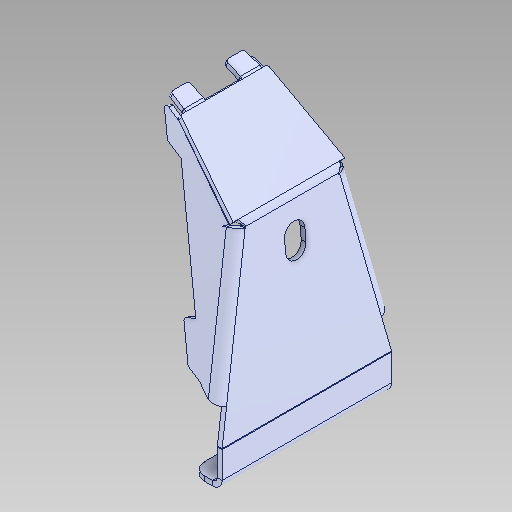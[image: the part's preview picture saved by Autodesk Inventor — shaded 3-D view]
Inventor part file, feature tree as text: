
AUTODESK INVENTOR PART (.ipt)
format: ipt  version: 2021 (Build 250183000, 183)  size: 224,256 bytes
history: native  units: in
note: dims shown in document units (in); Inventor stores cm internally (conversion verified against a paired STEP export)
features: fillet x1
ambient origin geometry x8: Origin, YZ Plane, XZ Plane, XY Plane, X Axis, Y Axis, Z Axis, Center Point
bodies: Solid1 (feature_tree)
feature tree (1):
  fillet  "Fillet2"  [1 undecoded]
note: 1 required parameter value undecoded (feature->parameter linkage not recoverable at this tier; creation-order binding heuristic only, values carry confidence <= 0.55)
